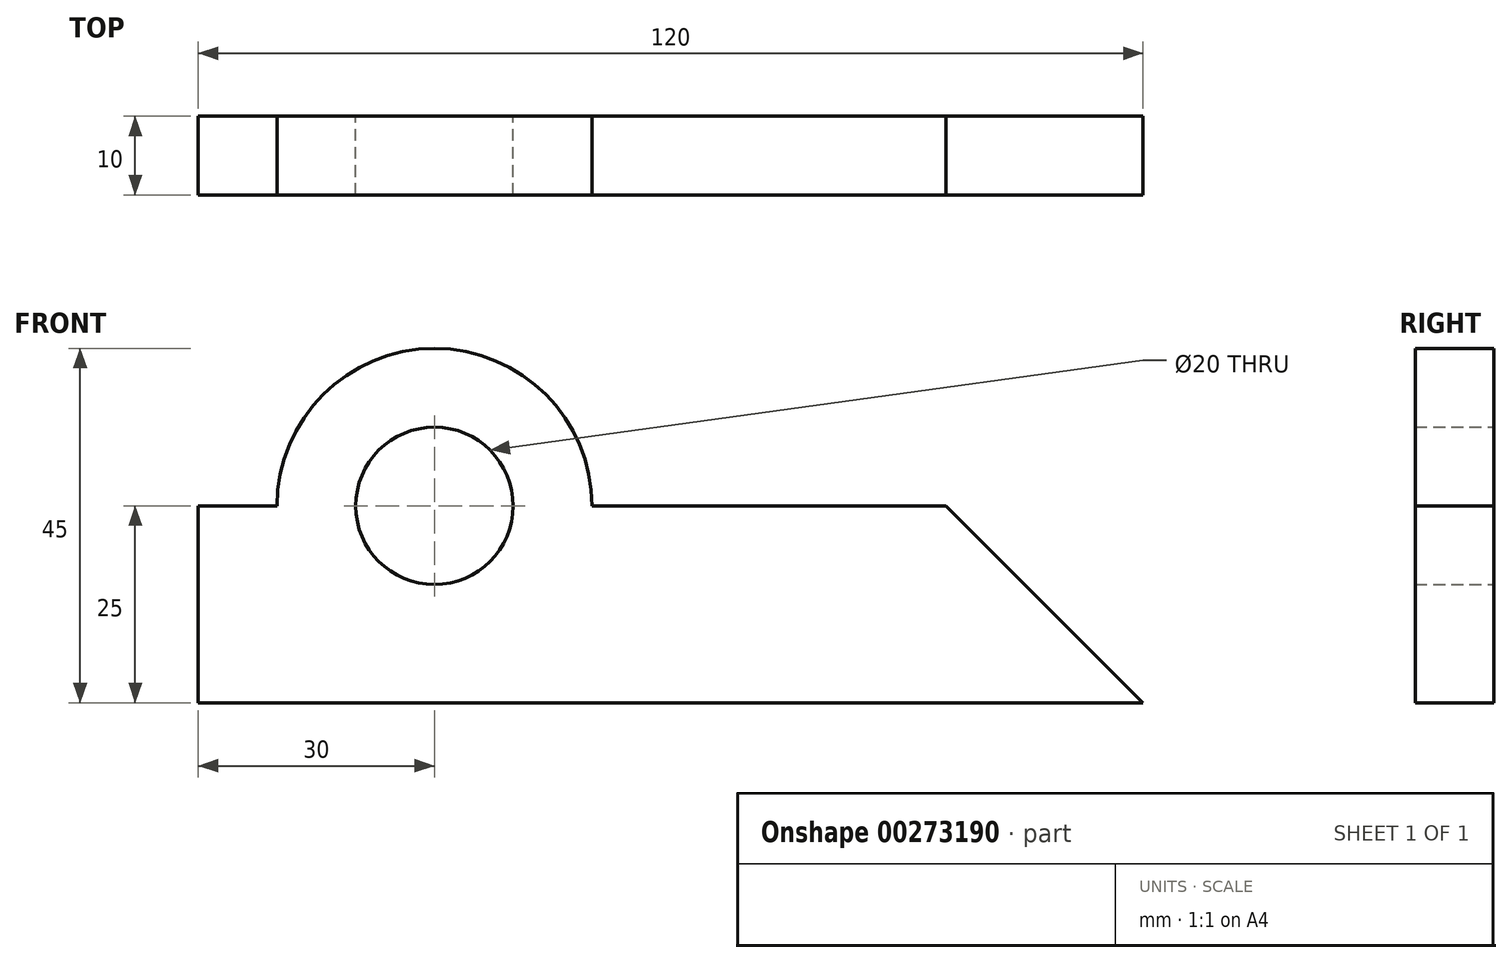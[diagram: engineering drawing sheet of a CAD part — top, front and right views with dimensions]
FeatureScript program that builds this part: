
annotation { "Feature Type Name" : "Feature", "Feature Type Description" : "" }
export const myFeature = defineFeature(function(context is Context, id is Id, definition is map)
    precondition{}
    {
        {
            var Q0;
            Q0=qCreatedBy(makeId("Front.planeOp"),FACE);
            var sketch = newSketch(context, id + "F0", { "sketchPlane" : qUnion([Q0])});
            skLineSegment(sketch, "E0", {"start": v(0, 0) * mm, "end": v(120, 0) * mm});
            skLineSegment(sketch, "E1", {"start": v(0, 0) * mm, "end": v(0, 25) * mm});
            skLineSegment(sketch, "E2", {"start": v(120, 0) * mm, "end": v(95, 25) * mm});
            skCircle(sketch, "E3", {"center": v(30, 25) * mm, "radius": 10 * mm});
            skLineSegment(sketch, "E4", {"start": v(0, 25) * mm, "end": v(10, 25) * mm});
            skLineSegment(sketch, "E5", {"start": v(95, 25) * mm, "end": v(50, 25) * mm});
            skArc(sketch, "E6", {"start": v(50, 25) * mm, "mid": v(30, 45) * mm, "end": v(10, 25) * mm});
            skSolve(sketch);
        }
        {
            var Q0;
            Q0=makeQuery(id+"F0.imprint","IMPRINT",FACE,{"disambiguationData":[TD([[makeQuery(id+"F0.imprint","IMPRINT",EDGE,{"derivedFrom":sQuery(id+"F0.wireOp",EDGE,"E0")}),1.0]])]});
            extrude(context, id + "F1", {"entities" : qUnion([Q0]), "depth" : 10 * mm});
        }
    });
